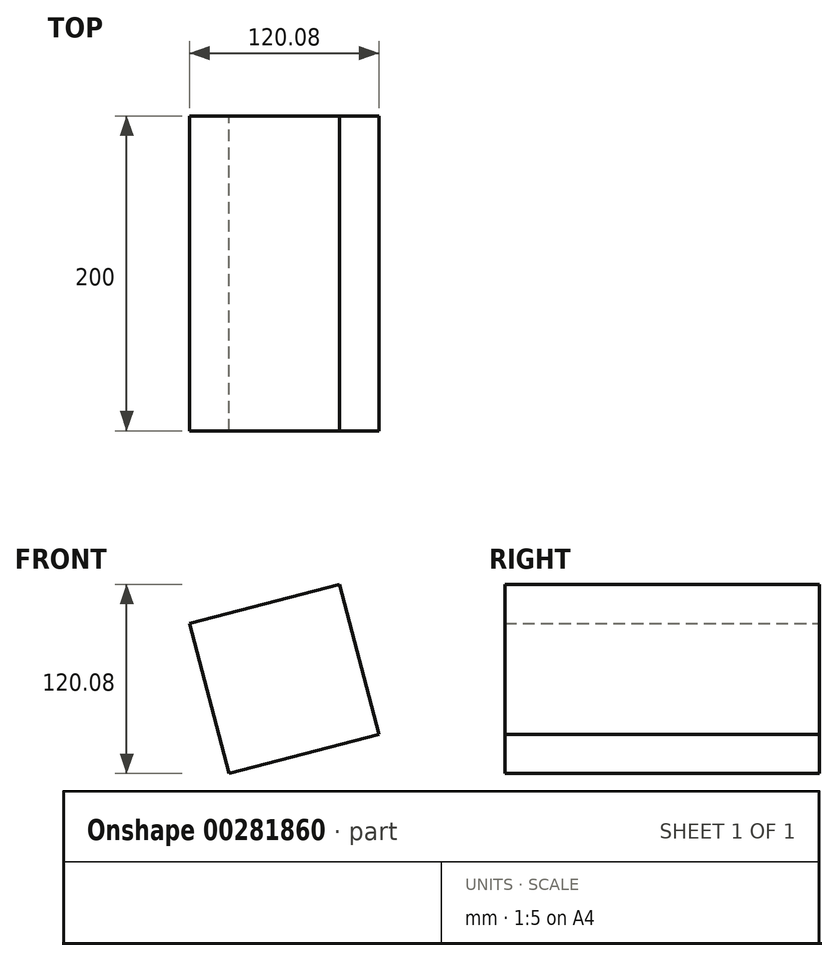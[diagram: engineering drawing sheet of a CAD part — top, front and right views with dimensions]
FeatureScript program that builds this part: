
annotation { "Feature Type Name" : "Feature", "Feature Type Description" : "" }
export const myFeature = defineFeature(function(context is Context, id is Id, definition is map)
    precondition{}
    {
        {
            var Q0;
            Q0=qCreatedBy(makeId("Front.planeOp"),FACE);
            var sketch = newSketch(context, id + "F0", { "sketchPlane" : qUnion([Q0])});
            skCircle(sketch, "E0.cCircle", {"center": v(0, 0) * mm, "radius": 69.56 * mm, "construction": true});
            skLineSegment(sketch, "E0.0", {"start": v(60.04, -35.12) * mm, "end": v(-35.12, -60.04) * mm});
            skLineSegment(sketch, "E0.1", {"start": v(-35.12, -60.04) * mm, "end": v(-60.04, 35.12) * mm});
            skLineSegment(sketch, "E0.2", {"start": v(-60.04, 35.12) * mm, "end": v(35.12, 60.04) * mm});
            skLineSegment(sketch, "E0.3", {"start": v(35.12, 60.04) * mm, "end": v(60.04, -35.12) * mm});
            skSolve(sketch);
        }
        {
            var Q0;
            Q0=makeQuery(id+"F0.imprint","IMPRINT",FACE,{"disambiguationData":[TD([[makeQuery(id+"F0.imprint","IMPRINT",EDGE,{"derivedFrom":sQuery(id+"F0.wireOp",EDGE,"E0.0")}),-1.0]])]});
            extrude(context, id + "F1", {"entities" : qUnion([Q0]), "depth" : 200 * mm});
        }
    });
